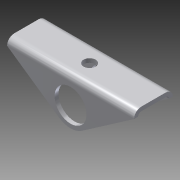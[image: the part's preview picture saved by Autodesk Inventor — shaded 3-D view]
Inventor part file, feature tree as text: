
AUTODESK INVENTOR PART (.ipt)
format: ipt  version: 2014 (Build 180170000, 170)  size: 156,160 bytes
history: native  units: in
note: dims shown in document units (in); Inventor stores cm internally (conversion verified against a paired STEP export)
features: sheet_metal_op x7, sketch x5, other x5, projected_geometry x1
ambient origin geometry x8: Origin, YZ Plane, XZ Plane, XY Plane, X Axis, Y Axis, Z Axis, Center Point
bodies: Solid1 (feature_tree)
feature tree (18):
  sheet_metal_op  "Face1"
  sheet_metal_op  "Flange1"
  sheet_metal_op  "Flange2"
  sketch  "Sketch1"  dims[d0=0.503in]
  other  "Plate1"
  sketch  "Sketch2"  dims[d1=0.3125in]
  other  "Plate2"
  sheet_metal_op  "Bend1"
  sheet_metal_op  "Corner1"
  sketch  "Sketch3"  dims[d2=1.0in]
  sketch  "Sketch4"  dims[d3=0.0625in]
  other  "Plate3"
  sheet_metal_op  "Bend2"
  sheet_metal_op  "Corner2"
  sketch  "Sketch5"  dims[d4=0.0625in d5=0.0625in d6=0.0312in d7=0.125in d8=0.0625in d9=0.5in d10=90.0deg d11=0.05in d12=0.25in d13=0.0625in d14=0.0625in d18=0.0625in d19=0.0in d35=0.19in d36=0.1875in d37=1.0in d39=0.0625in d40=0.0312in d41=0.125in d42=0.0625in d43=0.7515in d44=90.0deg d45=0.05in d46=0.25in d47=0.0625in d48=0.0625in d49=0.0625in d50=0.0in]
  projected_geometry  "Projected Loop1"
  other  "Cut1"
  other  "Cut2"
